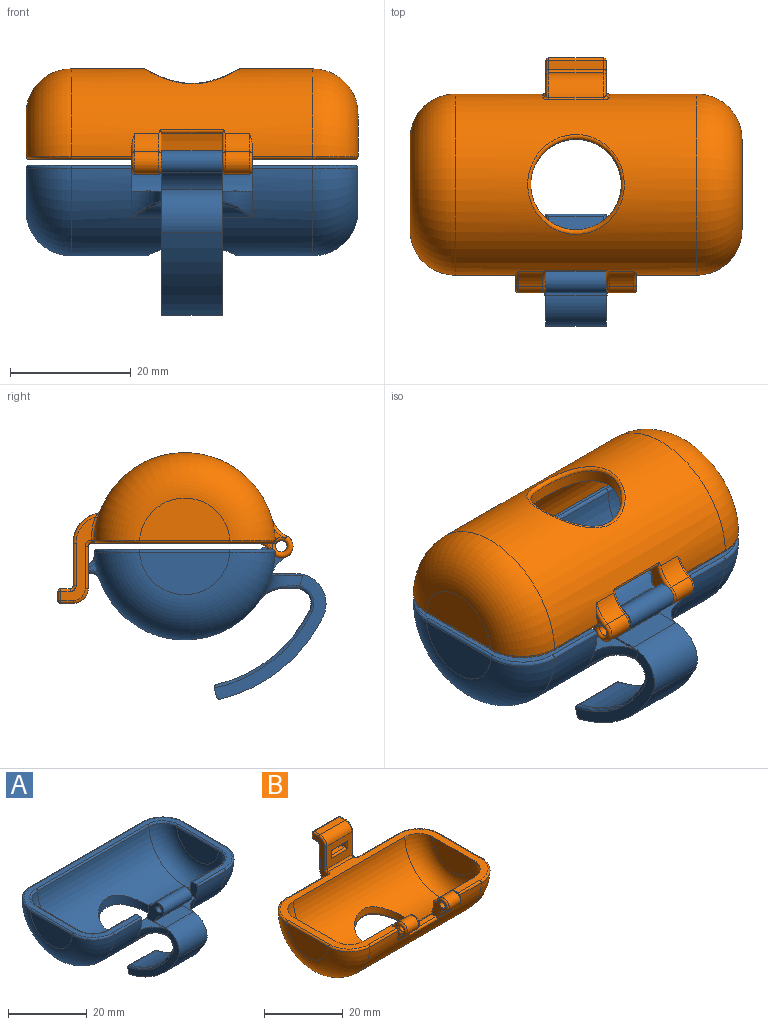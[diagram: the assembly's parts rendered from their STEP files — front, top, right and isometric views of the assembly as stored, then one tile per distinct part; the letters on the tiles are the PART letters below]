
ASSEMBLY  parts=2 mates=1
PART A: 85 faces, bbox 55.4x42.8x28.1 mm
  f0: cylinder r=15mm len=40mm, axis (1,0,0), area 1467.6mm2, adj f5,f6,f12,f18,f20,f25,f26,f27
  f1: plane 54x28.98mm, normal (0,0,1), area 193.9mm2, adj f18,f20,f67,f68,f69,f70,f71,f72
  f2: cylinder r=1.95mm len=10mm, axis (-1,0,0), area 70.7mm2, adj f13,f14,f16,f17
  f3: plane 14.97x7mm, normal (-1,0,0), area 80.9mm2, adj f11,f69
  f4: plane 14.97x7mm, normal (1,0,0), area 80.9mm2, adj f5,f78
  f5: torus R=7.5mm, axis (1,0,0), area 440.2mm2, adj f0,f4,f77,f79
  f6: torus R=7.5mm, axis (1,0,0), area 440.2mm2, adj f0,f7,f81,f83
  f7: plane 14.97x7mm, normal (-1,0,0), area 80.9mm2, adj f6,f82
  f8: plane 14.97x7mm, normal (1,0,0), area 80.9mm2, adj f9,f73
  f9: torus R=7.5mm, axis (1,0,0), area 255mm2, adj f8,f10,f72,f74
  f10: cylinder r=12.5mm len=40mm, axis (1,0,0), area 1312.7mm2, adj f9,f11,f12,f13,f14,f17,f18,f19
  f11: torus R=7.5mm, axis (1,0,0), area 255mm2, adj f3,f10,f68,f70
  f12: cylinder r=7.5mm len=15mm, axis (0,0,1), area 128.6mm2, adj f0,f10
  f13: plane 27.28x18.53mm, normal (1,0,0), area 81.6mm2, adj f2,f10,f15,f16,f17,f19,f32,f33
  f14: plane 27.28x18.53mm, normal (-1,0,0), area 81.6mm2, adj f2,f10,f15,f16,f17,f21,f32,f33
  f15: cylinder r=0.95mm len=10mm, axis (-1,0,0), area 59.7mm2, adj f13,f14
  f16: cylinder r=5mm len=10mm, axis (-1,0,0), area 37.7mm2, adj f2,f13,f14,f32
  f17: cylinder r=5mm len=10mm, axis (1,0,0), area 25.3mm2, adj f2,f10,f13,f14
  f18: plane 4.26x3.24mm, normal (-1,0,0), area 10.7mm2, adj f0,f1,f10,f19,f67,f76
  f19: plane 8.16x5.37mm, normal (0,0,1), area 18.7mm2, adj f10,f13,f18,f39
  f20: plane 4.26x3.24mm, normal (1,0,0), area 10.7mm2, adj f0,f1,f10,f21,f75,f84
  f21: plane 8.16x5.37mm, normal (0,0,1), area 18.7mm2, adj f10,f14,f20,f38
  f22: plane 4x1.44mm, normal (0,0,-1), area 5.8mm2, adj f27,f29,f46,f53
  f23: plane 4x0.53mm, normal (0,0,1), area 2.1mm2, adj f28,f30,f42,f49
  f24: plane 4x0.5mm, normal (0,1,0), area 2mm2, adj f29,f30,f44,f51
  f25: plane 2.49x1.63mm, normal (1,0,0), area 1.7mm2, adj f0,f48,f49,f51,f53,f54
  f26: plane 2.49x1.63mm, normal (-1,0,0), area 1.7mm2, adj f0,f41,f42,f44,f46,f47
  f27: cylinder r=1.5mm len=4mm, axis (1,0,0), area 7.4mm2, adj f0,f22,f47,f54
  f28: cylinder r=1.5mm len=4mm, axis (1,0,0), area 9.8mm2, adj f0,f23,f41,f48
  f29: cylinder r=0.5mm len=4mm, axis (-1,0,0), area 3.1mm2, adj f22,f24,f45,f52
  f30: cylinder r=0.5mm len=4mm, axis (1,0,0), area 3.1mm2, adj f23,f24,f43,f50
  f31: plane 10.28x2.06mm, normal (0,0,-1), area 19.6mm2, adj f36,f40,f56,f64
  f32: plane 10x3.95mm, normal (0,0,1), area 39.5mm2, adj f13,f14,f16,f37
  f33: cylinder r=25.5mm len=17.05mm, axis (-1,0,0), area 225.5mm2, adj f13,f14,f37,f66
  f34: plane 10x1.45mm, normal (0,0.97,-0.25), area 15mm2, adj f13,f14,f60,f66
  f35: cylinder r=23mm len=15.41mm, axis (-1,0,0), area 183.3mm2, adj f36,f59,f60,f61
  f36: cylinder r=2.5mm len=9.07mm, axis (-1,0,0), area 45.6mm2, adj f31,f35,f57,f58,f62,f63
  f37: cylinder r=5mm len=10mm, axis (-1,0,0), area 101.3mm2, adj f13,f14,f32,f33
  f38: torus R=20mm, axis (1,0,0), area 21.5mm2, adj f0,f14,f21,f55,f56,f57
  f39: torus R=20mm, axis (1,0,0), area 21.5mm2, adj f0,f13,f19,f63,f64,f65
  f40: cylinder r=5mm len=20mm, axis (1,0,0), area 69.5mm2, adj f0,f31,f55,f65
  f41: torus R=2mm, axis (1,0,0), area 1.7mm2, adj f0,f26,f28,f42
  f42: cylinder r=0.5mm len=0.53mm, axis (0,-1,0), area 0.4mm2, adj f23,f26,f41,f43
  f43: sphere r=0.5mm, area 0.4mm2, adj f30,f42,f44
  f44: cylinder r=0.5mm len=0.5mm, axis (0,0,1), area 0.4mm2, adj f24,f26,f43,f45
  f45: sphere r=0.5mm, area 0.4mm2, adj f29,f44,f46
  f46: cylinder r=0.5mm len=1.44mm, axis (0,1,0), area 1.1mm2, adj f22,f26,f45,f47
  f47: torus R=2mm, axis (1,0,0), area 1.2mm2, adj f0,f26,f27,f46
  f48: torus R=2mm, axis (1,0,0), area 1.7mm2, adj f0,f25,f28,f49
  f49: cylinder r=0.5mm len=0.53mm, axis (0,1,0), area 0.4mm2, adj f23,f25,f48,f50
  f50: sphere r=0.5mm, area 0.4mm2, adj f30,f49,f51
  f51: cylinder r=0.5mm len=0.5mm, axis (0,0,-1), area 0.4mm2, adj f24,f25,f50,f52
  f52: sphere r=0.5mm, area 0.4mm2, adj f29,f51,f53
  f53: cylinder r=0.5mm len=1.44mm, axis (0,-1,0), area 1.1mm2, adj f22,f25,f52,f54
  f54: torus R=2mm, axis (1,0,0), area 1.2mm2, adj f0,f25,f27,f53
  f55: bspline ~5.22x5.1mm, area 1.7mm2, adj f38,f40,f56
  f56: bspline ~4.51x1.73mm, area 1.5mm2, adj f31,f38,f55,f57
  f57: bspline ~1.34x0.63mm, area 0.4mm2, adj f36,f38,f56,f58
  f58: torus R=3mm, axis (1,0,0), area 3.8mm2, adj f14,f36,f57,f59
  f59: torus R=23.5mm, axis (1,0,0), area 16.3mm2, adj f14,f35,f58,f60
  f60: cylinder r=0.5mm len=10mm, axis (-1,0,0), area 7.7mm2, adj f13,f14,f34,f35,f59,f61
  f61: torus R=23.5mm, axis (1,0,0), area 16.3mm2, adj f13,f35,f60,f62
  f62: torus R=3mm, axis (1,0,0), area 3.8mm2, adj f13,f36,f61,f63
  f63: bspline ~1.73x0.7mm, area 0.4mm2, adj f36,f39,f62,f64
  f64: bspline ~4.51x1.73mm, area 1.5mm2, adj f31,f39,f63,f65
  f65: bspline ~5.22x5.1mm, area 1.7mm2, adj f39,f40,f64
  f66: cylinder r=0.5mm len=10mm, axis (-1,0,0), area 7.7mm2, adj f13,f14,f33,f34
  f67: cylinder r=0.5mm len=10mm, axis (1,0,0), area 7.7mm2, adj f1,f10,f18,f68
  f68: bspline ~6.77x6.73mm, area 6.3mm2, adj f1,f11,f67,f69
  f69: cylinder r=0.5mm len=14.97mm, axis (0,-1,0), area 11.8mm2, adj f1,f3,f68,f70
  f70: bspline ~6.77x6.73mm, area 6.3mm2, adj f1,f11,f69,f71
  f71: cylinder r=0.5mm len=40mm, axis (1,0,0), area 30.6mm2, adj f1,f10,f70,f72
  f72: bspline ~6.73x5.83mm, area 6.3mm2, adj f1,f9,f71,f73
  f73: cylinder r=0.5mm len=14.97mm, axis (0,1,0), area 11.8mm2, adj f1,f8,f72,f74
  f74: bspline ~6.77x6.73mm, area 6.3mm2, adj f1,f9,f73,f75
  f75: cylinder r=0.5mm len=10mm, axis (1,0,0), area 7.7mm2, adj f1,f10,f20,f74
  f76: cylinder r=0.5mm len=10mm, axis (1,0,0), area 8mm2, adj f0,f1,f18,f77
  f77: bspline ~9.21x9.18mm, area 9.2mm2, adj f1,f5,f76,f78
  f78: cylinder r=0.5mm len=14.97mm, axis (0,1,0), area 11.8mm2, adj f1,f4,f77,f79
  f79: bspline ~9.21x9.18mm, area 9.2mm2, adj f1,f5,f78,f80
  f80: cylinder r=0.5mm len=40mm, axis (1,0,0), area 32.1mm2, adj f0,f1,f79,f81
  f81: bspline ~9.21x9.18mm, area 9.2mm2, adj f1,f6,f80,f82
  f82: cylinder r=0.5mm len=14.97mm, axis (0,-1,0), area 11.8mm2, adj f1,f7,f81,f83
  f83: bspline ~9.21x9.18mm, area 9.2mm2, adj f1,f6,f82,f84
  f84: cylinder r=0.5mm len=10mm, axis (1,0,0), area 8mm2, adj f0,f1,f20,f83
PART B: 118 faces, bbox 55.2x39.3x26.6 mm
  f0: plane 1.84x1.79mm, normal (1,0,0), area 1mm2, adj f9,f56,f57
  f1: plane 1.36x1.33mm, normal (-1,0,0), area 0.5mm2, adj f15,f48,f49,f50
  f2: plane 13.82x5.62mm, normal (1,0,0), area 25.2mm2, adj f66,f70,f71,f76,f80,f81,f85,f86
  f3: cylinder r=12.5mm len=40mm, axis (1,0,0), area 1331.3mm2, adj f13,f14,f15,f16,f49,f55,f106,f108
  f4: cylinder r=1.95mm len=4mm, axis (1,0,0), area 28.3mm2, adj f25,f26,f50,f53
  f5: cylinder r=1.95mm len=4mm, axis (-1,0,0), area 28.3mm2, adj f20,f21,f56,f59
  f6: plane 15x7.5mm, normal (-1,0,0), area 88.4mm2, adj f14,f15
  f7: plane 14.97x7mm, normal (1,0,0), area 80.9mm2, adj f8,f41
  f8: torus R=7.5mm, axis (1,0,0), area 440.2mm2, adj f7,f9,f40,f42
  f9: cylinder r=15mm len=40mm, axis (1,0,0), area 1490.3mm2, adj f0,f8,f10,f20,f22,f26,f39,f43
  f10: torus R=7.5mm, axis (1,0,0), area 440.2mm2, adj f9,f11,f45,f47
  f11: plane 14.97x7mm, normal (-1,0,0), area 80.9mm2, adj f10,f46
  f12: plane 15x7.5mm, normal (1,0,0), area 88.4mm2, adj f13,f15
  f13: torus R=7.5mm, axis (1,0,0), area 263.6mm2, adj f3,f12,f15
  f14: torus R=7.5mm, axis (1,0,0), area 263.6mm2, adj f3,f6,f15
  f15: plane 54.19x30.18mm, normal (0,0,1), area 264.3mm2, adj f1,f3,f6,f12,f13,f14,f17,f39
  f16: cylinder r=7.5mm len=15mm, axis (0,0,1), area 96.2mm2, adj f3,f61
  f17: plane 1.36x1.33mm, normal (1,0,0), area 0.5mm2, adj f15,f43,f55,f56
  f18: plane 6.24x5.17mm, normal (-1,0,0), area 13mm2, adj f19,f27,f58,f59,f60,f112,f113
  f19: cylinder r=0.95mm len=4.52mm, axis (-1,0,0), area 26.9mm2, adj f18,f56,f116,f117
  f20: cylinder r=5mm len=4mm, axis (-1,0,0), area 16.2mm2, adj f5,f9,f57,f60
  f21: cylinder r=5mm len=4mm, axis (1,0,0), area 9mm2, adj f5,f55,f58,f108
  f22: plane 1.84x1.79mm, normal (-1,0,0), area 1mm2, adj f9,f50,f51
  f23: plane 6.24x5.17mm, normal (1,0,0), area 13mm2, adj f24,f27,f52,f53,f54,f109,f113
  f24: cylinder r=0.95mm len=4.52mm, axis (1,0,0), area 26.9mm2, adj f23,f50,f114,f115
  f25: cylinder r=5mm len=4mm, axis (-1,0,0), area 9mm2, adj f4,f49,f52,f106
  f26: cylinder r=5mm len=4mm, axis (1,0,0), area 16.2mm2, adj f4,f9,f51,f54
  f27: plane 10.06x1.6mm, normal (0,0,1), area 16mm2, adj f18,f23,f109,f111,f112,f113
  f28: plane 13.82x5.62mm, normal (-1,0,0), area 25.2mm2, adj f65,f68,f69,f74,f78,f79,f83,f84
  f29: plane 9x7.04mm, normal (0,1,0), area 48.4mm2, adj f62,f82,f87,f90,f102,f103,f104,f105
  f30: plane 9x7mm, normal (0,-1,0), area 48mm2, adj f38,f74,f75,f76,f98,f99,f100,f101
  f31: plane 5x1.5mm, normal (0,0,1), area 7.5mm2, adj f32,f33,f101,f104
  f32: plane 1.5x1.5mm, normal (-1,0,0), area 2.2mm2, adj f31,f34,f100,f102
  f33: plane 1.5x1.5mm, normal (1,0,0), area 2.2mm2, adj f31,f34,f99,f105
  f34: plane 5x1.5mm, normal (0,0,-1), area 7.5mm2, adj f32,f33,f98,f103
  f35: plane 9x1.5mm, normal (0,0,-1), area 13.5mm2, adj f72,f78,f81,f82
  f36: plane 9x1.5mm, normal (0,1,0), area 13.5mm2, adj f63,f68,f71,f72
  f37: plane 9x2mm, normal (0,0,1), area 18mm2, adj f38,f63,f65,f66
  f38: cylinder r=2.5mm len=9mm, axis (1,0,0), area 35.3mm2, adj f30,f37,f69,f70
  f39: cylinder r=0.5mm len=14.5mm, axis (1,0,0), area 11.6mm2, adj f9,f15,f40,f89
  f40: bspline ~9.18x7.95mm, area 9.2mm2, adj f8,f15,f39,f41
  f41: cylinder r=0.5mm len=14.97mm, axis (0,1,0), area 11.8mm2, adj f7,f15,f40,f42
  f42: bspline ~9.18x7.95mm, area 9.2mm2, adj f8,f15,f41,f43
  f43: cylinder r=0.5mm len=10mm, axis (1,0,0), area 8mm2, adj f9,f15,f17,f42,f116
  f44: cylinder r=0.5mm len=14.5mm, axis (1,0,0), area 11.6mm2, adj f9,f15,f45,f88
  f45: bspline ~9.21x9.18mm, area 9.2mm2, adj f10,f15,f44,f46
  f46: cylinder r=0.5mm len=14.97mm, axis (0,-1,0), area 11.8mm2, adj f11,f15,f45,f47
  f47: bspline ~9.21x9.18mm, area 9.2mm2, adj f10,f15,f46,f48
  f48: cylinder r=0.5mm len=10mm, axis (1,0,0), area 8mm2, adj f1,f9,f15,f47,f114
  f49: torus R=5.5mm, axis (-1,0,0), area 1.8mm2, adj f1,f3,f15,f25,f50,f106
  f50: torus R=1.45mm, axis (-1,0,0), area 10.2mm2, adj f1,f4,f22,f24,f49,f51,f114,f115
  f51: torus R=5.5mm, axis (-1,0,0), area 2.5mm2, adj f9,f22,f26,f50
  f52: torus R=5.5mm, axis (-1,0,0), area 1.8mm2, adj f23,f25,f53,f107
  f53: torus R=1.45mm, axis (-1,0,0), area 5mm2, adj f4,f23,f52,f54
  f54: torus R=5.5mm, axis (-1,0,0), area 3.5mm2, adj f9,f23,f26,f53,f113
  f55: torus R=5.5mm, axis (1,0,0), area 1.8mm2, adj f3,f15,f17,f21,f56,f108
  f56: torus R=1.45mm, axis (1,0,0), area 10.2mm2, adj f0,f5,f17,f19,f55,f57,f116,f117
  f57: torus R=5.5mm, axis (1,0,0), area 2.5mm2, adj f0,f9,f20,f56
  f58: torus R=5.5mm, axis (1,0,0), area 1.8mm2, adj f18,f21,f59,f110
  f59: torus R=1.45mm, axis (1,0,0), area 5mm2, adj f5,f18,f58,f60
  f60: torus R=5.5mm, axis (1,0,0), area 3.5mm2, adj f9,f18,f20,f59,f113
  f61: bspline ~16.56x16.01mm, area 46.1mm2, adj f9,f16
  f62: cylinder r=5mm len=9mm, axis (1,0,0), area 62.4mm2, adj f29,f91,f94,f97
  f63: cylinder r=0.5mm len=9mm, axis (-1,0,0), area 7.1mm2, adj f36,f37,f64,f67
  f64: sphere r=0.5mm, area 0.4mm2, adj f63,f65,f68
  f65: cylinder r=0.5mm len=2mm, axis (0,-1,0), area 1.6mm2, adj f28,f37,f64,f69
  f66: cylinder r=0.5mm len=2mm, axis (0,1,0), area 1.6mm2, adj f2,f37,f67,f70
  f67: sphere r=0.5mm, area 0.4mm2, adj f63,f66,f71
  f68: cylinder r=0.5mm len=1.5mm, axis (0,0,1), area 1.2mm2, adj f28,f36,f64,f73
  f69: torus R=2mm, axis (1,0,0), area 2.9mm2, adj f28,f38,f65,f74
  f70: torus R=2mm, axis (-1,0,0), area 2.9mm2, adj f2,f38,f66,f76
  f71: cylinder r=0.5mm len=1.5mm, axis (0,0,-1), area 1.2mm2, adj f2,f36,f67,f77
  f72: cylinder r=0.5mm len=9mm, axis (1,0,0), area 7.1mm2, adj f35,f36,f73,f77
  f73: sphere r=0.5mm, area 0.4mm2, adj f68,f72,f78
  f74: cylinder r=0.5mm len=7mm, axis (0,0,1), area 5.5mm2, adj f28,f30,f69,f79
  f75: cylinder r=0.5mm len=9mm, axis (-1,0,0), area 7.1mm2, adj f15,f30,f79,f80
  f76: cylinder r=0.5mm len=7mm, axis (0,0,1), area 5.5mm2, adj f2,f30,f70,f80
  f77: sphere r=0.5mm, area 0.4mm2, adj f71,f72,f81
  f78: cylinder r=0.5mm len=1.5mm, axis (0,1,0), area 1.2mm2, adj f28,f35,f73,f83
  f79: torus R=1mm, axis (1,0,0), area 0.8mm2, adj f28,f74,f75,f84
  f80: torus R=1mm, axis (-1,0,0), area 0.8mm2, adj f2,f75,f76,f85
  f81: cylinder r=0.5mm len=1.5mm, axis (0,-1,0), area 1.2mm2, adj f2,f35,f77,f86
  f82: cylinder r=0.5mm len=9mm, axis (-1,0,0), area 7.1mm2, adj f29,f35,f83,f86
  f83: torus R=1mm, axis (1,0,0), area 0.8mm2, adj f28,f78,f82,f87
  f84: cylinder r=0.5mm len=0.5mm, axis (0,1,0), area 0mm2, adj f15,f28,f79,f88
  f85: cylinder r=0.5mm len=0.5mm, axis (0,1,0), area 0mm2, adj f2,f15,f80,f89
  f86: torus R=1mm, axis (-1,0,0), area 0.8mm2, adj f2,f81,f82,f90
  f87: cylinder r=0.5mm len=7.04mm, axis (0,0,-1), area 5.5mm2, adj f28,f29,f83,f91
  f88: bspline ~1.23x1.17mm, area 0.8mm2, adj f15,f44,f84,f92
  f89: bspline ~1.22x1.12mm, area 0.8mm2, adj f15,f39,f85,f93
  f90: cylinder r=0.5mm len=7.04mm, axis (0,0,1), area 5.5mm2, adj f2,f29,f86,f94
  f91: torus R=4.5mm, axis (1,0,0), area 5mm2, adj f28,f62,f87,f95
  f92: torus R=15.5mm, axis (1,0,0), area 3mm2, adj f9,f28,f88,f95
  f93: torus R=15.5mm, axis (-1,0,0), area 3mm2, adj f2,f9,f89,f96
  f94: torus R=4.5mm, axis (-1,0,0), area 5mm2, adj f2,f62,f90,f96
  f95: bspline ~1.4x1.12mm, area 0.8mm2, adj f9,f91,f92,f97
  f96: bspline ~1.35x1.2mm, area 0.8mm2, adj f9,f93,f94,f97
  f97: cylinder r=0.5mm len=9mm, axis (-1,0,0), area 4.6mm2, adj f9,f62,f95,f96
  f98: cylinder r=0.5mm len=6mm, axis (-1,0,0), area 4.3mm2, adj f30,f34,f99,f100
  f99: cylinder r=0.5mm len=2.5mm, axis (0,0,-1), area 1.6mm2, adj f30,f33,f98,f101
  f100: cylinder r=0.5mm len=2.5mm, axis (0,0,1), area 1.6mm2, adj f30,f32,f98,f101
  f101: cylinder r=0.5mm len=6mm, axis (1,0,0), area 4.3mm2, adj f30,f31,f99,f100
  f102: cylinder r=0.5mm len=2.5mm, axis (0,0,-1), area 1.6mm2, adj f29,f32,f103,f104
  f103: cylinder r=0.5mm len=6mm, axis (1,0,0), area 4.3mm2, adj f29,f34,f102,f105
  f104: cylinder r=0.5mm len=6mm, axis (-1,0,0), area 4.3mm2, adj f29,f31,f102,f105
  f105: cylinder r=0.5mm len=2.5mm, axis (0,0,1), area 1.6mm2, adj f29,f33,f103,f104
  f106: cylinder r=0.5mm len=4mm, axis (1,0,0), area 2mm2, adj f3,f25,f49,f107
  f107: sphere r=0.5mm, area 0.3mm2, adj f52,f106,f109
  f108: cylinder r=0.5mm len=4mm, axis (1,0,0), area 2mm2, adj f3,f21,f55,f110
  f109: torus R=13mm, axis (-1,0,0), area 3.3mm2, adj f3,f23,f27,f107,f111
  f110: sphere r=0.5mm, area 0.3mm2, adj f58,f108,f112
  f111: cylinder r=0.5mm len=11mm, axis (1,0,0), area 6.3mm2, adj f3,f27,f109,f112
  f112: torus R=13mm, axis (1,0,0), area 3.3mm2, adj f3,f18,f27,f110,f111
  f113: cylinder r=0.5mm len=10.51mm, axis (1,0,0), area 9.7mm2, adj f9,f18,f23,f27,f54,f60
  f114: bspline ~0.79x0.77mm, area 0.3mm2, adj f24,f48,f50,f115
  f115: bspline ~0.52x0.46mm, area 0mm2, adj f9,f24,f50,f114
  f116: bspline ~0.79x0.77mm, area 0.3mm2, adj f19,f43,f56,f117
  f117: bspline ~0.52x0.44mm, area 0mm2, adj f9,f19,f56,f116
PLACE A at identity
PLACE B rot(axis=(0,1,0),180deg) t=(0,0,1)mm
MATE revolute B.f4 <-> A.f2  axis (-1,0,0) through (5,-16,0.5)mm
